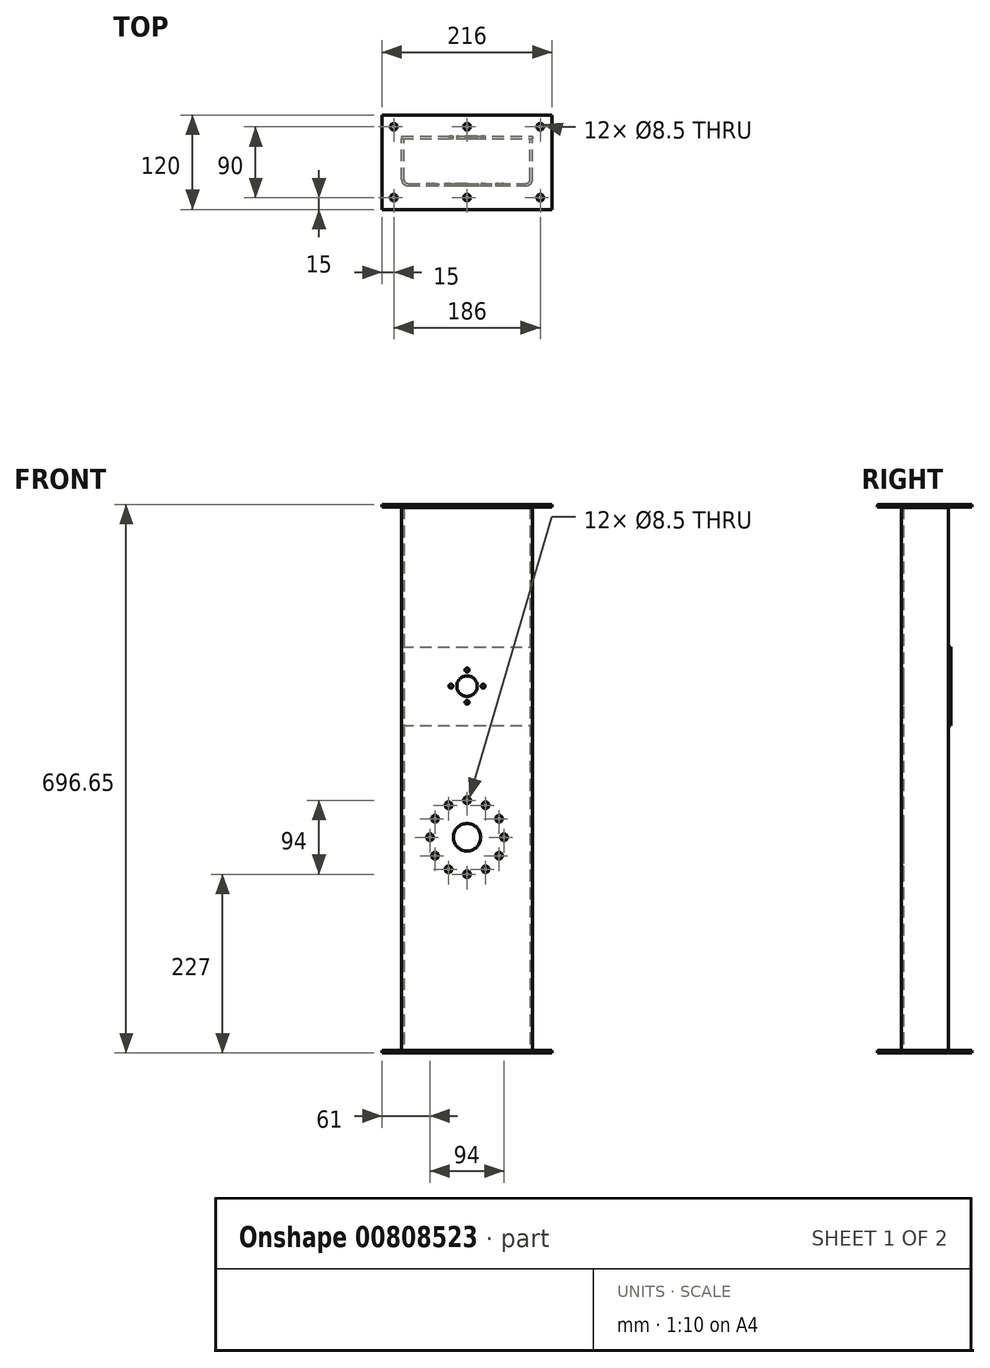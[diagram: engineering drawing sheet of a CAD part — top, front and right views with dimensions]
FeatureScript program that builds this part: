
annotation { "Feature Type Name" : "Feature", "Feature Type Description" : "" }
export const myFeature = defineFeature(function(context is Context, id is Id, definition is map)
    precondition{}
    {
        {
            var Q0;
            Q0=qCreatedBy(makeId("Top.planeOp"),FACE);
            var sketch = newSketch(context, id + "F0", { "sketchPlane" : qUnion([Q0])});
            skLineSegment(sketch, "E0", {"start": v(-75, 0) * mm, "end": v(75, 0) * mm});
            skLineSegment(sketch, "E1", {"start": v(-80, 5) * mm, "end": v(-80, 57) * mm});
            skLineSegment(sketch, "E2", {"start": v(80, 5) * mm, "end": v(80, 57) * mm});
            skLineSegment(sketch, "E3.0", {"start": v(83, 5) * mm, "end": v(83, 57) * mm});
            skLineSegment(sketch, "E4.0", {"start": v(-83, 5) * mm, "end": v(-83, 57) * mm});
            skLineSegment(sketch, "E5.0", {"start": v(-75, -3) * mm, "end": v(75, -3) * mm});
            skLineSegment(sketch, "E6", {"start": v(-83, 57) * mm, "end": v(-80, 57) * mm});
            skLineSegment(sketch, "E7", {"start": v(80, 57) * mm, "end": v(83, 57) * mm});
            skPoint(sketch, "E8.visualSharp", {"position": v(-80, 0) * mm});
            skArc(sketch, "E8.filletArc", {"start": v(-80, 5) * mm, "mid": v(-78.54, 1.46) * mm, "end": v(-75, 0) * mm});
            skPoint(sketch, "E9.visualSharp", {"position": v(-83, -3) * mm});
            skArc(sketch, "E9.filletArc", {"start": v(-83, 5) * mm, "mid": v(-80.66, -0.66) * mm, "end": v(-75, -3) * mm});
            skPoint(sketch, "E10.visualSharp", {"position": v(80, 0) * mm});
            skArc(sketch, "E10.filletArc", {"start": v(75, 0) * mm, "mid": v(78.54, 1.46) * mm, "end": v(80, 5) * mm});
            skPoint(sketch, "E11.visualSharp", {"position": v(83, -3) * mm});
            skArc(sketch, "E11.filletArc", {"start": v(75, -3) * mm, "mid": v(80.66, -0.66) * mm, "end": v(83, 5) * mm});
            skLineSegment(sketch, "E12.bottom", {"start": v(-108, 87) * mm, "end": v(108, 87) * mm});
            skLineSegment(sketch, "E12.top", {"start": v(-108, -33) * mm, "end": v(108, -33) * mm});
            skLineSegment(sketch, "E12.left", {"start": v(-108, 87) * mm, "end": v(-108, -33) * mm});
            skLineSegment(sketch, "E12.right", {"start": v(108, 87) * mm, "end": v(108, -33) * mm});
            skCircle(sketch, "E13", {"center": v(-93, 72) * mm, "radius": 4.25 * mm});
            skCircle(sketch, "E14", {"center": v(-93, -18) * mm, "radius": 4.25 * mm});
            skCircle(sketch, "E15", {"center": v(93, 72) * mm, "radius": 4.25 * mm});
            skCircle(sketch, "E16", {"center": v(93, -18) * mm, "radius": 4.25 * mm});
            skCircle(sketch, "E17", {"center": v(0, -18) * mm, "radius": 4.25 * mm});
            skCircle(sketch, "E18", {"center": v(0, 72) * mm, "radius": 4.25 * mm});
            skSolve(sketch);
        }
        {
            var Q0;
            Q0=makeQuery(id+"F0.imprint","IMPRINT",FACE,{"disambiguationData":[TD([[makeQuery(id+"F0.imprint","IMPRINT",EDGE,{"derivedFrom":sQuery(id+"F0.wireOp",EDGE,"E0")}),-1.0]])]});
            extrude(context, id + "F1", {"entities" : qUnion([Q0]), "depth" : 690 * mm, "offsetDistance" : 25 * mm});
        }
        {
            var Q0;
            Q0=makeQuery(id+"F0.imprint","IMPRINT",FACE,{"disambiguationData":[TD([[makeQuery(id+"F0.imprint","IMPRINT",EDGE,{"derivedFrom":sQuery(id+"F0.wireOp",EDGE,"E0")}),1.0]])]});
            var Q1;
            Q1=makeQuery(id+"F0.imprint","IMPRINT",FACE,{"disambiguationData":[TD([[makeQuery(id+"F0.imprint","IMPRINT",EDGE,{"derivedFrom":sQuery(id+"F0.wireOp",EDGE,"E0")}),-1.0]])]});
            extrude(context, id + "F2", {"entities" : qUnion([Q0, Q1]), "oppositeDirection" : true, "depth" : 3 * mm, "offsetDistance" : 25 * mm});
        }
        {
            var Q0;
            Q0=makeQuery(id+"F1.opExtrude","SWEPT_FACE",FACE,{"disambiguationData":[OSD([sQuery(id+"F0.wireOp",EDGE,"E5.0")])]});
            var sketch = newSketch(context, id + "F3", { "sketchPlane" : qUnion([Q0])});
            skCircle(sketch, "E19", {"center": v(0, 463) * mm, "radius": 13 * mm});
            skLineSegment(sketch, "E20.0", {"start": v(-108, -3) * mm, "end": v(108, -3) * mm, "construction": true});
            skCircle(sketch, "E21", {"center": v(0, 271) * mm, "radius": 17.5 * mm});
            skCircle(sketch, "E22", {"center": v(0, 463) * mm, "radius": 20.5 * mm, "construction": true});
            skCircle(sketch, "E23", {"center": v(0, 483.5) * mm, "radius": 2.5 * mm});
            skCircle(sketch, "E24.1.0", {"center": v(-20.5, 463) * mm, "radius": 2.5 * mm});
            skCircle(sketch, "E24.2.0", {"center": v(0, 442.5) * mm, "radius": 2.5 * mm});
            skCircle(sketch, "E24.3.0", {"center": v(20.5, 463) * mm, "radius": 2.5 * mm});
            skCircle(sketch, "E25", {"center": v(0, 271) * mm, "radius": 47 * mm, "construction": true});
            skCircle(sketch, "E26", {"center": v(0, 318) * mm, "radius": 4.25 * mm});
            skCircle(sketch, "E27.1.0", {"center": v(-23.5, 311.7) * mm, "radius": 4.25 * mm});
            skCircle(sketch, "E27.2.0", {"center": v(-40.7, 294.5) * mm, "radius": 4.25 * mm});
            skCircle(sketch, "E27.3.0", {"center": v(-47, 271) * mm, "radius": 4.25 * mm});
            skCircle(sketch, "E28.1.4.0", {"center": v(-40.7, 247.5) * mm, "radius": 4.25 * mm});
            skCircle(sketch, "E28.1.5.0", {"center": v(-23.5, 230.3) * mm, "radius": 4.25 * mm});
            skCircle(sketch, "E28.1.6.0", {"center": v(0, 224) * mm, "radius": 4.25 * mm});
            skCircle(sketch, "E28.1.7.0", {"center": v(23.5, 230.3) * mm, "radius": 4.25 * mm});
            skCircle(sketch, "E29.1.8.0", {"center": v(40.7, 247.5) * mm, "radius": 4.25 * mm});
            skCircle(sketch, "E29.1.9.0", {"center": v(47, 271) * mm, "radius": 4.25 * mm});
            skCircle(sketch, "E29.1.10.0", {"center": v(40.7, 294.5) * mm, "radius": 4.25 * mm});
            skCircle(sketch, "E29.1.11.0", {"center": v(23.5, 311.7) * mm, "radius": 4.25 * mm});
            skSolve(sketch);
        }
        {
            var Q0;
            Q0=makeQuery(id+"F3.imprint","IMPRINT",FACE,{"disambiguationData":[TD([[makeQuery(id+"F3.imprint","IMPRINT",EDGE,{"derivedFrom":sQuery(id+"F3.wireOp",EDGE,"E23")}),1.0]])]});
            var Q1;
            Q1=makeQuery(id+"F3.imprint","IMPRINT",FACE,{"disambiguationData":[TD([[makeQuery(id+"F3.imprint","IMPRINT",EDGE,{"derivedFrom":sQuery(id+"F3.wireOp",EDGE,"E24.3.0")}),1.0]])]});
            var Q2;
            Q2=makeQuery(id+"F3.imprint","IMPRINT",FACE,{"disambiguationData":[TD([[makeQuery(id+"F3.imprint","IMPRINT",EDGE,{"derivedFrom":sQuery(id+"F3.wireOp",EDGE,"E24.2.0")}),1.0]])]});
            var Q3;
            Q3=makeQuery(id+"F3.imprint","IMPRINT",FACE,{"disambiguationData":[TD([[makeQuery(id+"F3.imprint","IMPRINT",EDGE,{"derivedFrom":sQuery(id+"F3.wireOp",EDGE,"E24.1.0")}),1.0]])]});
            var Q4;
            Q4=makeQuery(id+"F3.imprint","IMPRINT",FACE,{"disambiguationData":[TD([[makeQuery(id+"F3.imprint","IMPRINT",EDGE,{"derivedFrom":sQuery(id+"F3.wireOp",EDGE,"E19")}),1.0]])]});
            var Q5;
            Q5=makeQuery(id+"F3.imprint","IMPRINT",FACE,{"disambiguationData":[TD([[makeQuery(id+"F3.imprint","IMPRINT",EDGE,{"derivedFrom":sQuery(id+"F3.wireOp",EDGE,"E29.1.11.0")}),1.0]])]});
            var Q6;
            Q6=makeQuery(id+"F3.imprint","IMPRINT",FACE,{"disambiguationData":[TD([[makeQuery(id+"F3.imprint","IMPRINT",EDGE,{"derivedFrom":sQuery(id+"F3.wireOp",EDGE,"E26")}),1.0]])]});
            var Q7;
            Q7=makeQuery(id+"F3.imprint","IMPRINT",FACE,{"disambiguationData":[TD([[makeQuery(id+"F3.imprint","IMPRINT",EDGE,{"derivedFrom":sQuery(id+"F3.wireOp",EDGE,"E27.1.0")}),1.0]])]});
            var Q8;
            Q8=makeQuery(id+"F3.imprint","IMPRINT",FACE,{"disambiguationData":[TD([[makeQuery(id+"F3.imprint","IMPRINT",EDGE,{"derivedFrom":sQuery(id+"F3.wireOp",EDGE,"E29.1.10.0")}),1.0]])]});
            var Q9;
            Q9=makeQuery(id+"F3.imprint","IMPRINT",FACE,{"disambiguationData":[TD([[makeQuery(id+"F3.imprint","IMPRINT",EDGE,{"derivedFrom":sQuery(id+"F3.wireOp",EDGE,"E29.1.9.0")}),1.0]])]});
            var Q10;
            Q10=makeQuery(id+"F3.imprint","IMPRINT",FACE,{"disambiguationData":[TD([[makeQuery(id+"F3.imprint","IMPRINT",EDGE,{"derivedFrom":sQuery(id+"F3.wireOp",EDGE,"E29.1.8.0")}),1.0]])]});
            var Q11;
            Q11=makeQuery(id+"F3.imprint","IMPRINT",FACE,{"disambiguationData":[TD([[makeQuery(id+"F3.imprint","IMPRINT",EDGE,{"derivedFrom":sQuery(id+"F3.wireOp",EDGE,"E28.1.7.0")}),1.0]])]});
            var Q12;
            Q12=makeQuery(id+"F3.imprint","IMPRINT",FACE,{"disambiguationData":[TD([[makeQuery(id+"F3.imprint","IMPRINT",EDGE,{"derivedFrom":sQuery(id+"F3.wireOp",EDGE,"E28.1.6.0")}),1.0]])]});
            var Q13;
            Q13=makeQuery(id+"F3.imprint","IMPRINT",FACE,{"disambiguationData":[TD([[makeQuery(id+"F3.imprint","IMPRINT",EDGE,{"derivedFrom":sQuery(id+"F3.wireOp",EDGE,"E28.1.5.0")}),1.0]])]});
            var Q14;
            Q14=makeQuery(id+"F3.imprint","IMPRINT",FACE,{"disambiguationData":[TD([[makeQuery(id+"F3.imprint","IMPRINT",EDGE,{"derivedFrom":sQuery(id+"F3.wireOp",EDGE,"E28.1.4.0")}),1.0]])]});
            var Q15;
            Q15=makeQuery(id+"F3.imprint","IMPRINT",FACE,{"disambiguationData":[TD([[makeQuery(id+"F3.imprint","IMPRINT",EDGE,{"derivedFrom":sQuery(id+"F3.wireOp",EDGE,"E27.3.0")}),1.0]])]});
            var Q16;
            Q16=makeQuery(id+"F3.imprint","IMPRINT",FACE,{"disambiguationData":[TD([[makeQuery(id+"F3.imprint","IMPRINT",EDGE,{"derivedFrom":sQuery(id+"F3.wireOp",EDGE,"E27.2.0")}),1.0]])]});
            var Q17;
            Q17=makeQuery(id+"F3.imprint","IMPRINT",FACE,{"disambiguationData":[TD([[makeQuery(id+"F3.imprint","IMPRINT",EDGE,{"derivedFrom":sQuery(id+"F3.wireOp",EDGE,"E21")}),1.0]])]});
            extrude(context, id + "F4", {"entities" : qUnion([Q0, Q1, Q2, Q3, Q4, Q5, Q6, Q7, Q8, Q9, Q10, Q11, Q12, Q13, Q14, Q15, Q16, Q17]), "operationType" : NewBodyOperationType.REMOVE, "oppositeDirection" : true, "depth" : 25 * mm, "offsetDistance" : 25 * mm});
        }
        {
            var Q0;
            Q0=makeQuery(id+"F2.opExtrude","SWEPT_BODY",BODY,{"disambiguationData":[OSD([sQuery(id+"F0.wireOp",EDGE,"E12.bottom"),sQuery(id+"F0.wireOp",EDGE,"E12.top"),sQuery(id+"F0.wireOp",EDGE,"E12.left"),sQuery(id+"F0.wireOp",EDGE,"E12.right"),sQuery(id+"F0.wireOp",EDGE,"E13"),sQuery(id+"F0.wireOp",EDGE,"E14"),sQuery(id+"F0.wireOp",EDGE,"E15"),sQuery(id+"F0.wireOp",EDGE,"E16"),sQuery(id+"F0.wireOp",EDGE,"E17"),sQuery(id+"F0.wireOp",EDGE,"E18")])]});
            transform(context, id + "F5", {"entities" : qUnion([Q0]), "transformType" : TransformType.TRANSLATION_3D, "dx" : 0 * mm, "dy" : 0 * mm, "dz" : 693.65 * mm, "makeCopy" : true});
        }
        {
            var Q0;
            Q0=makeQuery(id+"F1.opExtrude","SWEPT_FACE",FACE,{"disambiguationData":[OSD([sQuery(id+"F0.wireOp",EDGE,"E6")])]});
            var sketch = newSketch(context, id + "F6", { "sketchPlane" : qUnion([Q0])});
            skCircle(sketch, "E30.0", {"center": v(0, 463) * mm, "radius": 13 * mm});
            skLineSegment(sketch, "E31.bottom", {"start": v(83, 413) * mm, "end": v(-83, 413) * mm});
            skLineSegment(sketch, "E31.top", {"start": v(83, 513) * mm, "end": v(-83, 513) * mm});
            skLineSegment(sketch, "E31.left", {"start": v(83, 413) * mm, "end": v(83, 513) * mm});
            skLineSegment(sketch, "E31.right", {"start": v(-83, 413) * mm, "end": v(-83, 513) * mm});
            skCircle(sketch, "E32.0", {"center": v(0, 483.5) * mm, "radius": 2.5 * mm});
            skCircle(sketch, "E33.0", {"center": v(20.5, 463) * mm, "radius": 2.5 * mm});
            skCircle(sketch, "E34.0", {"center": v(0, 442.5) * mm, "radius": 2.5 * mm});
            skCircle(sketch, "E35.0", {"center": v(-20.5, 463) * mm, "radius": 2.5 * mm});
            skSolve(sketch);
        }
        {
            var Q0;
            Q0=makeQuery(id+"F6.imprint","IMPRINT",FACE,{"disambiguationData":[TD([[makeQuery(id+"F6.imprint","IMPRINT",EDGE,{"derivedFrom":sQuery(id+"F6.wireOp",EDGE,"E30.0")}),-1.0]])]});
            var Q1;
            {var subQ0=sQuery(id+"F6.wireOp",EDGE,"E31.left");Q1=makeQuery(id+"F6.imprint","IMPRINT",FACE,{"disambiguationData":[TD([[makeQuery(id+"F6.imprint","IMPRINT",EDGE,{"derivedFrom":subQ0}),-1.0]])]});}
            extrude(context, id + "F7", {"entities" : qUnion([Q0, Q1]), "depth" : 3 * mm, "offsetDistance" : 25 * mm});
        }
    });
